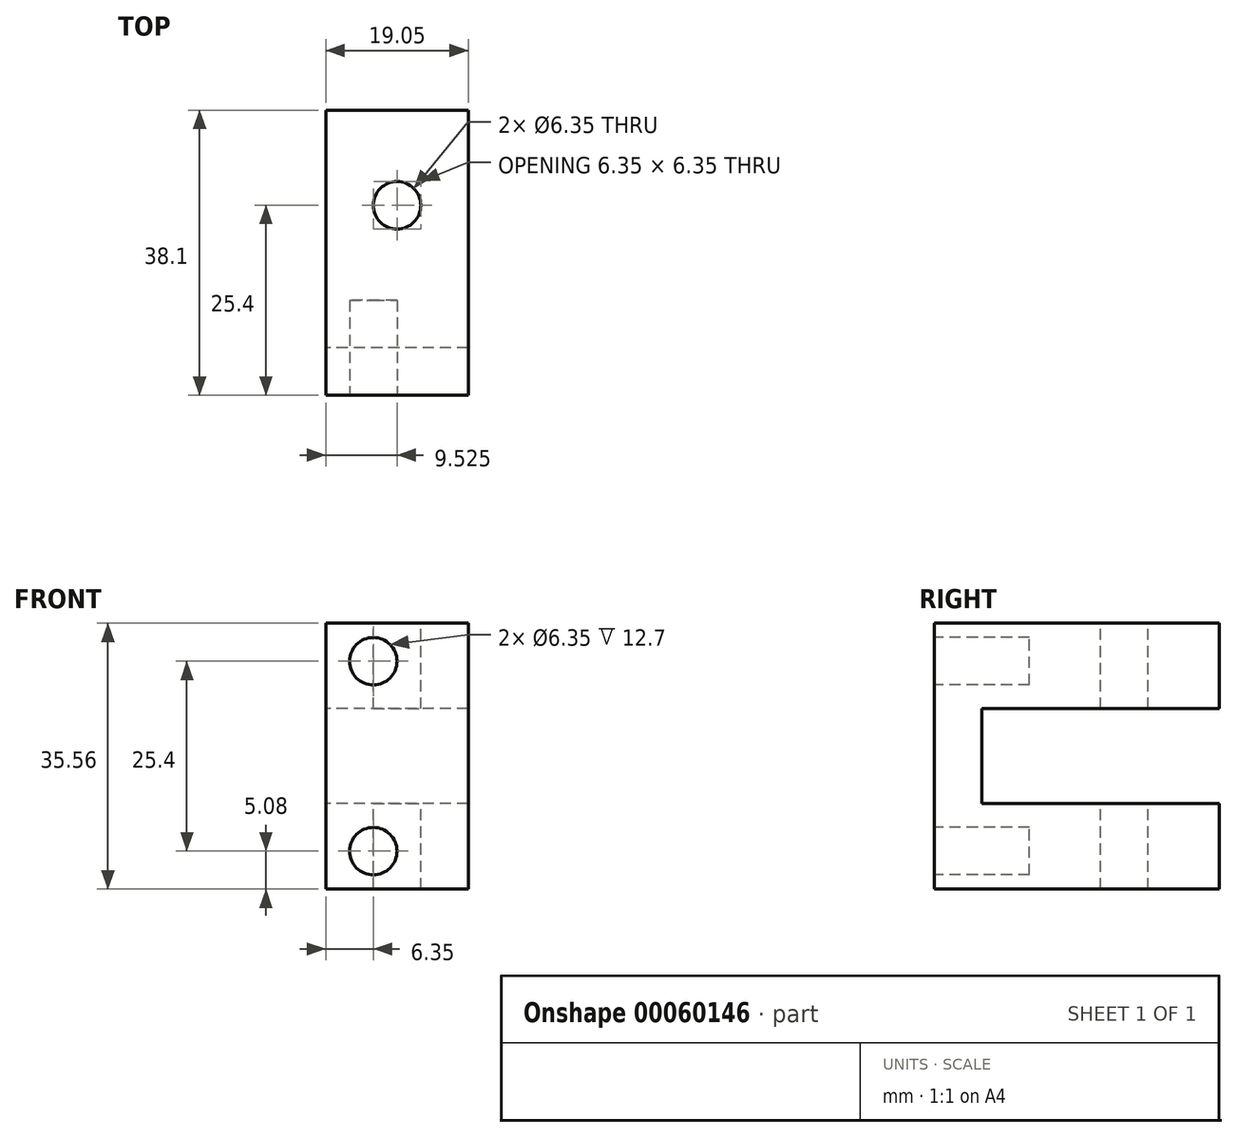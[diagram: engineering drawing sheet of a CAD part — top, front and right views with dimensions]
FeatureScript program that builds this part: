
annotation { "Feature Type Name" : "Feature", "Feature Type Description" : "" }
export const myFeature = defineFeature(function(context is Context, id is Id, definition is map)
    precondition{}
    {
        {
            var Q0;
            Q0=qCreatedBy(makeId("Top.planeOp"),FACE);
            var sketch = newSketch(context, id + "F0", { "sketchPlane" : qUnion([Q0])});
            skLineSegment(sketch, "E0.bottom", {"start": v(0, 0) * mm, "end": v(19.05, 0) * mm});
            skLineSegment(sketch, "E0.top", {"start": v(0, 38.1) * mm, "end": v(19.05, 38.1) * mm});
            skLineSegment(sketch, "E0.left", {"start": v(0, 0) * mm, "end": v(0, 38.1) * mm});
            skLineSegment(sketch, "E0.right", {"start": v(19.05, 0) * mm, "end": v(19.05, 38.1) * mm});
            skSolve(sketch);
        }
        {
            var Q0;
            Q0 = qSketchRegion(id + "F0", true);
            extrude(context, id + "F1", {"entities" : qUnion([Q0]), "endBound" : BoundingType.SYMMETRIC, "depth" : 35.56 * mm});
        }
        {
            var Q0;
            Q0=makeQuery(id+"F1.opExtrude","SWEPT_FACE",FACE,{"disambiguationData":[OSD([sQuery(id+"F0.wireOp",EDGE,"E0.left")])]});
            var sketch = newSketch(context, id + "F2", { "sketchPlane" : qUnion([Q0])});
            skLineSegment(sketch, "E1.bottom", {"start": v(-38.1, 6.35) * mm, "end": v(-6.35, 6.35) * mm});
            skLineSegment(sketch, "E1.top", {"start": v(-38.1, -6.35) * mm, "end": v(-6.35, -6.35) * mm});
            skLineSegment(sketch, "E1.left", {"start": v(-38.1, 6.35) * mm, "end": v(-38.1, -6.35) * mm});
            skLineSegment(sketch, "E1.right", {"start": v(-6.35, 6.35) * mm, "end": v(-6.35, -6.35) * mm});
            skSolve(sketch);
        }
        {
            var Q0;
            Q0 = qSketchRegion(id + "F2", true);
            extrude(context, id + "F3", {"entities" : qUnion([Q0]), "operationType" : NewBodyOperationType.REMOVE, "oppositeDirection" : true, "depth" : 25.4 * mm});
        }
        {
            var Q0;
            Q0=makeQuery(id+"F1.opExtrude","CAP_FACE",FACE,{"disambiguationData":[OSD([sQuery(id+"F0.wireOp",EDGE,"E0.bottom"),sQuery(id+"F0.wireOp",EDGE,"E0.top"),sQuery(id+"F0.wireOp",EDGE,"E0.left"),sQuery(id+"F0.wireOp",EDGE,"E0.right")])],"isStart":false});
            var sketch = newSketch(context, id + "F4", { "sketchPlane" : qUnion([Q0])});
            skCircle(sketch, "E2", {"center": v(9.52, 25.4) * mm, "radius": 3.18 * mm});
            skSolve(sketch);
        }
        {
            var Q0;
            Q0 = qSketchRegion(id + "F4", true);
            extrude(context, id + "F5", {"entities" : qUnion([Q0]), "operationType" : NewBodyOperationType.REMOVE, "oppositeDirection" : true, "depth" : 76.2 * mm});
        }
        {
            var Q0;
            Q0=makeQuery(id+"F1.opExtrude","SWEPT_FACE",FACE,{"disambiguationData":[OSD([sQuery(id+"F0.wireOp",EDGE,"E0.bottom")])]});
            var sketch = newSketch(context, id + "F6", { "sketchPlane" : qUnion([Q0])});
            skCircle(sketch, "E3", {"center": v(6.35, 12.7) * mm, "radius": 3.18 * mm});
            skCircle(sketch, "E4", {"center": v(6.35, -12.7) * mm, "radius": 3.18 * mm});
            skSolve(sketch);
        }
        {
            var Q0;
            Q0 = qSketchRegion(id + "F6", true);
            extrude(context, id + "F7", {"entities" : qUnion([Q0]), "operationType" : NewBodyOperationType.REMOVE, "oppositeDirection" : true, "depth" : 12.7 * mm});
        }
    });
